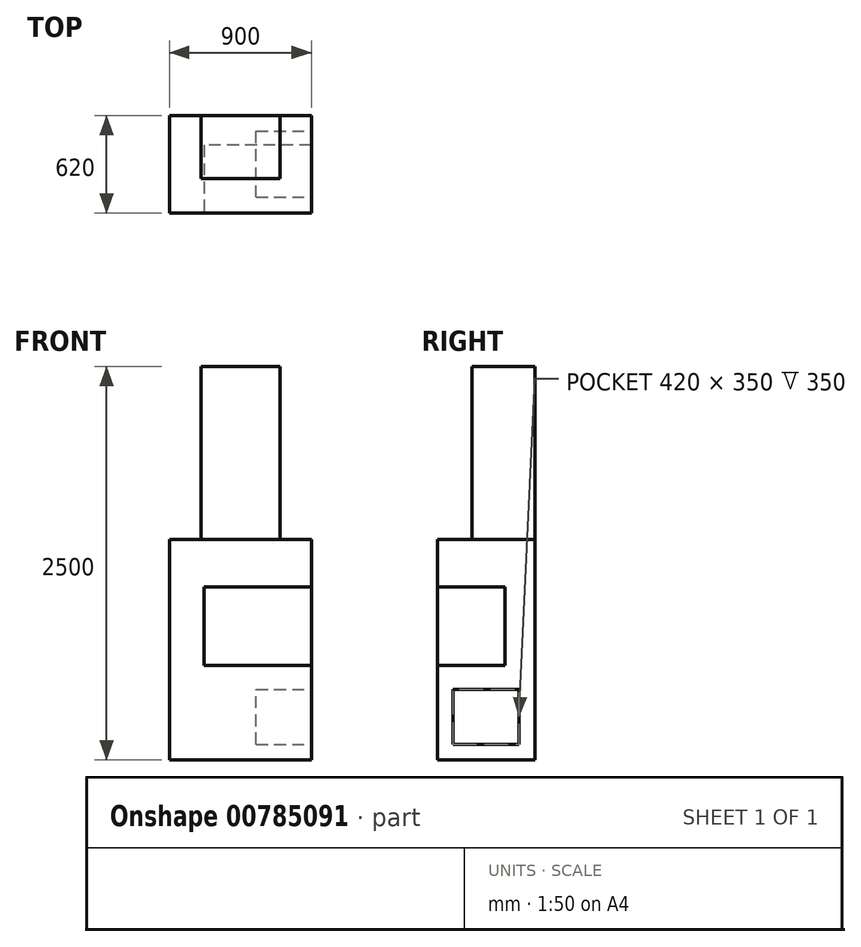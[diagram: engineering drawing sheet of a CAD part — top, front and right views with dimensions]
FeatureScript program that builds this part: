
annotation { "Feature Type Name" : "Feature", "Feature Type Description" : "" }
export const myFeature = defineFeature(function(context is Context, id is Id, definition is map)
    precondition{}
    {
        {
            var Q0;
            Q0=qCreatedBy(makeId("Top.planeOp"),FACE);
            var sketch = newSketch(context, id + "F0", { "sketchPlane" : qUnion([Q0])});
            skLineSegment(sketch, "E0.bottom", {"start": v(-447.7, 228.76) * mm, "end": v(452.3, 228.76) * mm});
            skLineSegment(sketch, "E0.top", {"start": v(-447.7, -391.24) * mm, "end": v(452.3, -391.24) * mm});
            skLineSegment(sketch, "E0.left", {"start": v(-447.7, 228.76) * mm, "end": v(-447.7, -391.24) * mm});
            skLineSegment(sketch, "E0.right", {"start": v(452.3, 228.76) * mm, "end": v(452.3, -391.24) * mm});
            skSolve(sketch);
        }
        {
            var Q0;
            Q0=makeQuery(id+"F0.imprint","IMPRINT",FACE,{"disambiguationData":[TD([[makeQuery(id+"F0.imprint","IMPRINT",EDGE,{"derivedFrom":sQuery(id+"F0.wireOp",EDGE,"E0.bottom")}),-1.0]])]});
            extrude(context, id + "F1", {"entities" : qUnion([Q0]), "depth" : 1400 * mm, "offsetDistance" : 25 * mm});
        }
        {
            var Q0;
            Q0=makeQuery(id+"F1.opExtrude","SWEPT_FACE",FACE,{"disambiguationData":[OSD([sQuery(id+"F0.wireOp",EDGE,"E0.top")])]});
            var sketch = newSketch(context, id + "F2", { "sketchPlane" : qUnion([Q0])});
            skLineSegment(sketch, "E1.bottom", {"start": v(452.3, 600) * mm, "end": v(-229.7, 600) * mm});
            skLineSegment(sketch, "E1.top", {"start": v(452.3, 1100) * mm, "end": v(-229.7, 1100) * mm});
            skLineSegment(sketch, "E1.left", {"start": v(452.3, 600) * mm, "end": v(452.3, 1100) * mm});
            skLineSegment(sketch, "E1.right", {"start": v(-229.7, 600) * mm, "end": v(-229.7, 1100) * mm});
            skSolve(sketch);
        }
        {
            var Q0;
            Q0=makeQuery(id+"F2.imprint","IMPRINT",FACE,{"disambiguationData":[TD([[makeQuery(id+"F2.imprint","IMPRINT",EDGE,{"derivedFrom":sQuery(id+"F2.wireOp",EDGE,"E1.bottom")}),-1.0]])]});
            extrude(context, id + "F3", {"entities" : qUnion([Q0]), "operationType" : NewBodyOperationType.REMOVE, "oppositeDirection" : true, "depth" : 430 * mm, "offsetDistance" : 25 * mm});
        }
        {
            var Q0;
            Q0=makeQuery(id+"F1.opExtrude","CAP_FACE",FACE,{"disambiguationData":[OSD([sQuery(id+"F0.wireOp",EDGE,"E0.bottom"),sQuery(id+"F0.wireOp",EDGE,"E0.top"),sQuery(id+"F0.wireOp",EDGE,"E0.left"),sQuery(id+"F0.wireOp",EDGE,"E0.right")])],"isStart":false});
            var sketch = newSketch(context, id + "F4", { "sketchPlane" : qUnion([Q0])});
            skLineSegment(sketch, "E2", {"start": v(-247.7, 228.76) * mm, "end": v(-247.7, -171.24) * mm});
            skLineSegment(sketch, "E3", {"start": v(-247.7, -171.24) * mm, "end": v(252.3, -171.24) * mm});
            skLineSegment(sketch, "E4", {"start": v(252.3, -171.24) * mm, "end": v(252.3, 228.76) * mm});
            skLineSegment(sketch, "E5", {"start": v(252.3, 228.76) * mm, "end": v(-247.7, 228.76) * mm});
            skSolve(sketch);
        }
        {
            var Q0;
            Q0=makeQuery(id+"F4.imprint","IMPRINT",FACE,{"disambiguationData":[TD([[makeQuery(id+"F4.imprint","IMPRINT",EDGE,{"derivedFrom":sQuery(id+"F4.wireOp",EDGE,"E2")}),1.0]])]});
            extrude(context, id + "F5", {"entities" : qUnion([Q0]), "operationType" : NewBodyOperationType.ADD, "depth" : 1100 * mm, "offsetDistance" : 25 * mm});
        }
        {
            var Q0;
            Q0=makeQuery(id+"F1.opExtrude","SWEPT_FACE",FACE,{"disambiguationData":[OSD([sQuery(id+"F0.wireOp",EDGE,"E0.right")])]});
            var sketch = newSketch(context, id + "F6", { "sketchPlane" : qUnion([Q0])});
            skLineSegment(sketch, "E6.bottom", {"start": v(-291.24, 100) * mm, "end": v(128.76, 100) * mm});
            skLineSegment(sketch, "E6.top", {"start": v(-291.24, 450) * mm, "end": v(128.76, 450) * mm});
            skLineSegment(sketch, "E6.left", {"start": v(-291.24, 100) * mm, "end": v(-291.24, 450) * mm});
            skLineSegment(sketch, "E6.right", {"start": v(128.76, 100) * mm, "end": v(128.76, 450) * mm});
            skSolve(sketch);
        }
        {
            var Q0;
            Q0=makeQuery(id+"F6.imprint","IMPRINT",FACE,{"disambiguationData":[TD([[makeQuery(id+"F6.imprint","IMPRINT",EDGE,{"derivedFrom":sQuery(id+"F6.wireOp",EDGE,"E6.bottom")}),1.0]])]});
            extrude(context, id + "F7", {"entities" : qUnion([Q0]), "operationType" : NewBodyOperationType.REMOVE, "oppositeDirection" : true, "depth" : 350 * mm, "offsetDistance" : 25 * mm});
        }
    });
